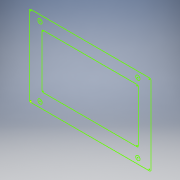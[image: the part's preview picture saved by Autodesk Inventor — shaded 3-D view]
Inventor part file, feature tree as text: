
AUTODESK INVENTOR PART (.ipt)
format: ipt  version: 2019 (Build 230136000, 136)  size: 96,768 bytes
history: native  units: in
note: dims shown in document units (in); Inventor stores cm internally (conversion verified against a paired STEP export)
features: sketch x1
ambient origin geometry x8: Origin, YZ Plane, XZ Plane, XY Plane, X Axis, Y Axis, Z Axis, Center Point
feature tree (1):
  sketch  "Sketch3"
